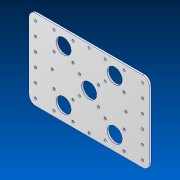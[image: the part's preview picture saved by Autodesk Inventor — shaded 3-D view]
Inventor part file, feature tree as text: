
AUTODESK INVENTOR PART (.ipt)
format: ipt  version: 2022.2 (Build 262287000, 287)  size: 154,112 bytes
history: native  units: in
note: dims shown in document units (in); Inventor stores cm internally (conversion verified against a paired STEP export)
features: other x1, extrude x1, hole x1, sketch x1
ambient origin geometry x8: Origin, YZ Plane, XZ Plane, XY Plane, X Axis, Y Axis, Z Axis, Center Point
bodies: Body1 (feature_tree)
feature tree (4):
  other  "Motor Bracket Outer Panel.ipt"
  extrude  "Extrusion1"  Depth=0.125in TaperAngle=0.0deg
  hole  "Hole1"  [1 undecoded]
  sketch  "Sketch1"  dims[d0=0.3937in d1=0.125in d2=0.0in d3=0.17in d4=0.75in d5=0.375in d6=0.25in d7=0.5635in d8=1.0in d9=0.8108in]
note: 1 required parameter value undecoded (feature->parameter linkage not recoverable at this tier; creation-order binding heuristic only, values carry confidence <= 0.55)
